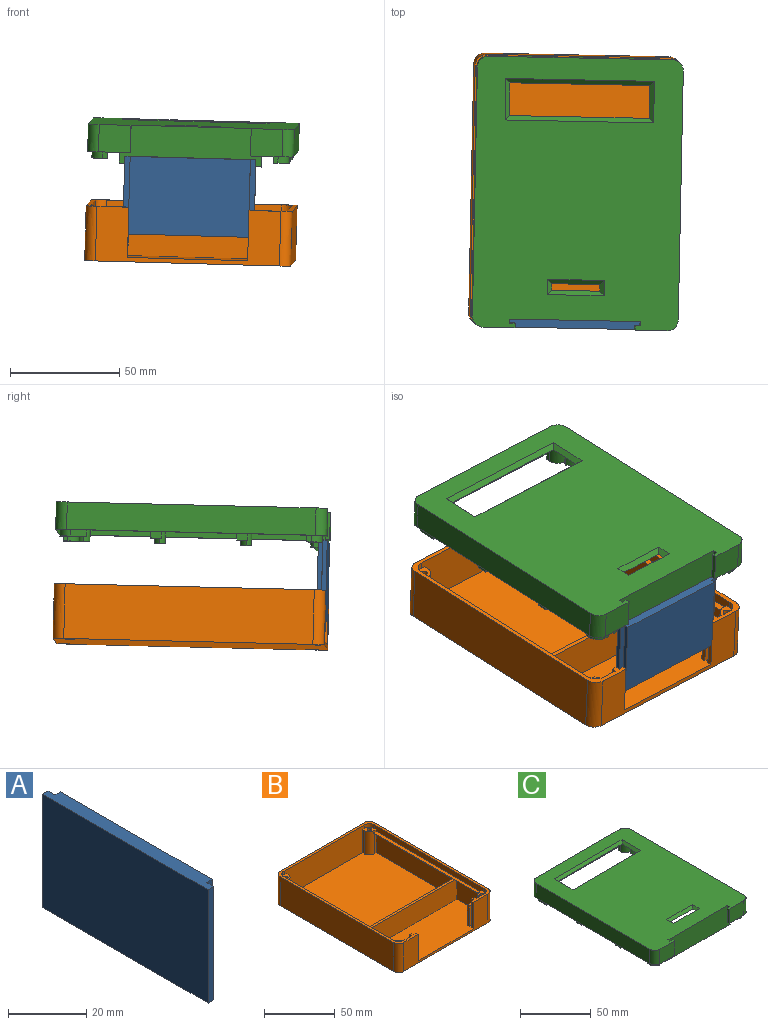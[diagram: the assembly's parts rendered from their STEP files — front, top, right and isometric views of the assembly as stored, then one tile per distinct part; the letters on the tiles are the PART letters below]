
ASSEMBLY  parts=3 mates=2
PART A: 10 faces, bbox 4x60x35.5 mm
  f0: plane 60x35.5mm, normal (-1,0,0), area 2130mm2, adj f1,f7,f8,f9
  f1: plane 35.5x2mm, normal (0,-1,0), area 71mm2, adj f0,f2,f8,f9
  f2: plane 35.5x2.5mm, normal (1,0,0), area 88.7mm2, adj f1,f3,f8,f9
  f3: plane 35.5x2mm, normal (0,-1,0), area 71mm2, adj f2,f4,f8,f9
  f4: plane 55x35.5mm, normal (1,0,0), area 1952.5mm2, adj f3,f5,f8,f9
  f5: plane 35.5x2mm, normal (0,1,0), area 71mm2, adj f4,f6,f8,f9
  f6: plane 35.5x2.5mm, normal (1,0,0), area 88.7mm2, adj f5,f7,f8,f9
  f7: plane 35.5x2mm, normal (0,1,0), area 71mm2, adj f0,f6,f8,f9
  f8: plane 60x4mm, normal (0,0,-1), area 230mm2, adj f0,f1,f2,f3,f4,f5,f6,f7
  f9: plane 60x4mm, normal (0,0,1), area 230mm2, adj f0,f1,f2,f3,f4,f5,f6,f7
PART B: 78 faces, bbox 94.2x124x25 mm
  f0: plane 124x94.2mm, normal (0,0,1), area 756.8mm2, adj f1,f3,f17,f20,f21,f22,f23,f24
  f1: plane 84.2x25mm, normal (0,-1,0), area 840mm2, adj f0,f5,f25,f30,f31,f68,f69
  f2: plane 18x5mm, normal (0,1,0), area 90mm2, adj f5,f62,f73,f75
  f3: plane 23x7.6mm, normal (0,1,0), area 134.8mm2, adj f0,f5,f38,f40,f55,f62
  f4: plane 25x15.5mm, normal (1,0,0), area 387.5mm2, adj f5,f8,f15,f59
  f5: plane 90.2x34mm, normal (0,0,1), area 2879.1mm2, adj f1,f2,f3,f4,f6,f12,f15,f20
  f6: plane 25x15.5mm, normal (-1,0,0), area 387.5mm2, adj f5,f7,f12,f59
  f7: plane 106.21x3.01mm, normal (-0.71,0,-0.71), area 442.7mm2, adj f6,f12,f18,f26,f44,f46,f48,f58
  f8: plane 106.21x3.01mm, normal (0.71,0,-0.71), area 442.7mm2, adj f4,f9,f14,f15,f45,f47,f49,f58
  f9: plane 17.5x2mm, normal (0,-1,0), area 33mm2, adj f8,f14,f19,f49
  f10: plane 2x1.5mm, normal (0,-1,0), area 3mm2, adj f17,f37,f44,f48
  f11: plane 2x1.5mm, normal (0,1,0), area 3mm2, adj f21,f43,f45,f47
  f12: plane 17.5x2mm, normal (0,1,0), area 33mm2, adj f5,f6,f7,f46
  f13: plane 2x1.5mm, normal (0,-1,0), area 3mm2, adj f21,f34,f45,f49
  f14: plane 79x15.5mm, normal (1,0,0), area 1224.5mm2, adj f8,f9,f19,f58
  f15: plane 17.5x2mm, normal (0,1,0), area 33mm2, adj f4,f5,f8,f47
  f16: plane 2x1.5mm, normal (0,1,0), area 3mm2, adj f17,f40,f44,f46
  f17: plane 110x4.5mm, normal (-1,0,0), area 489mm2, adj f0,f10,f16,f37,f40,f44,f55,f57
  f18: plane 17.5x2mm, normal (0,-1,0), area 33mm2, adj f7,f19,f26,f48
  f19: plane 90.2x86mm, normal (0,0,1), area 7669.9mm2, adj f9,f14,f18,f26,f27,f32,f35,f48
  f20: plane 23x7.6mm, normal (0,1,0), area 134.8mm2, adj f0,f5,f41,f43,f54,f61
  f21: plane 110x4.5mm, normal (1,0,0), area 489mm2, adj f0,f11,f13,f34,f43,f45,f54,f56
  f22: plane 114x25mm, normal (1,0,0), area 2850mm2, adj f0,f25,f28,f31
  f23: plane 84.2x25mm, normal (0,1,0), area 2105mm2, adj f0,f25,f28,f29
  f24: plane 114x25mm, normal (-1,0,0), area 2850mm2, adj f0,f25,f29,f30
  f25: plane 124x94.2mm, normal (0,0,-1), area 11404.9mm2, adj f1,f22,f23,f24,f28,f29,f30,f31
  f26: plane 79x15.5mm, normal (-1,0,0), area 1224.5mm2, adj f7,f18,f19,f58
  f27: plane 80.2x23mm, normal (0,-1,0), area 1764.6mm2, adj f0,f19,f32,f34,f35,f37,f56,f57
  f28: cylinder r=5mm len=25mm, axis (0,0,-1), area 196.3mm2, adj f0,f22,f23,f25
  f29: cylinder r=5mm len=25mm, axis (0,0,1), area 196.3mm2, adj f0,f23,f24,f25
  f30: cylinder r=5mm len=25mm, axis (0,0,-1), area 196.3mm2, adj f0,f1,f24,f25
  f31: cylinder r=5mm len=25mm, axis (0,0,1), area 196.3mm2, adj f0,f1,f22,f25
  f32: plane 20x2mm, normal (1,0,0), area 40mm2, adj f19,f27,f34,f49
  f33: cylinder r=1.5mm len=19mm, axis (0,0,-1), area 179.1mm2, adj f34,f50
  f34: plane 7x7mm, normal (0,0,1), area 31.2mm2, adj f13,f21,f27,f32,f33,f49,f56
  f35: plane 20x2mm, normal (-1,0,0), area 40mm2, adj f19,f27,f37,f48
  f36: cylinder r=1.5mm len=19mm, axis (0,0,-1), area 179.1mm2, adj f37,f51
  f37: plane 7x7mm, normal (0,0,1), area 31.2mm2, adj f10,f17,f27,f35,f36,f48,f57
  f38: plane 20x2mm, normal (-1,0,0), area 40mm2, adj f3,f5,f40,f46
  f39: cylinder r=1.5mm len=19mm, axis (0,0,-1), area 179.1mm2, adj f40,f52
  f40: plane 7x7mm, normal (0,0,1), area 31.2mm2, adj f3,f16,f17,f38,f39,f46,f55
  f41: plane 20x2mm, normal (1,0,0), area 40mm2, adj f5,f20,f43,f47
  f42: cylinder r=1.5mm len=19mm, axis (0,0,-1), area 179.1mm2, adj f43,f53
  f43: plane 7x7mm, normal (0,0,1), area 31.2mm2, adj f11,f20,f21,f41,f42,f47,f54
  f44: plane 106.2x3mm, normal (0,0,1), area 318.1mm2, adj f7,f10,f16,f17,f46,f48
  f45: plane 106.2x3mm, normal (0,0,1), area 318.1mm2, adj f8,f11,f13,f21,f47,f49
  f46: cylinder r=5mm len=20mm, axis (0,0,1), area 156.6mm2, adj f5,f7,f12,f16,f38,f40,f44
  f47: cylinder r=5mm len=20mm, axis (0,0,1), area 156.6mm2, adj f5,f8,f11,f15,f41,f43,f45
  f48: cylinder r=5mm len=20mm, axis (0,0,1), area 156.6mm2, adj f7,f10,f18,f19,f35,f37,f44
  f49: cylinder r=5mm len=20mm, axis (0,0,1), area 156.6mm2, adj f8,f9,f13,f19,f32,f34,f45
  f50: cone r=4.5mm half-angle=45deg, axis (0,0,-1), area 80mm2, adj f25,f33
  f51: cone r=4.5mm half-angle=45deg, axis (0,0,-1), area 80mm2, adj f25,f36
  f52: cone r=4.5mm half-angle=45deg, axis (0,0,-1), area 80mm2, adj f25,f39
  f53: cone r=4.5mm half-angle=45deg, axis (0,0,-1), area 80mm2, adj f25,f42
  f54: cylinder r=5mm len=5mm, axis (0,0,1), area 23.6mm2, adj f0,f20,f21,f43
  f55: cylinder r=5mm len=5mm, axis (0,0,-1), area 23.6mm2, adj f0,f3,f17,f40
  f56: cylinder r=5mm len=5mm, axis (0,0,-1), area 23.6mm2, adj f0,f21,f27,f34
  f57: cylinder r=5mm len=5mm, axis (0,0,1), area 23.6mm2, adj f0,f17,f27,f37
  f58: plane 90.2x18mm, normal (0,1,0), area 1617.4mm2, adj f7,f8,f14,f19,f26,f60
  f59: plane 90.2x18mm, normal (0,-1,0), area 1617.4mm2, adj f4,f5,f6,f7,f8,f60
  f60: plane 85.2x2mm, normal (0,0,1), area 170.4mm2, adj f7,f8,f58,f59
  f61: plane 23x4mm, normal (-1,0,0), area 82mm2, adj f0,f5,f20,f63,f76,f77
  f62: plane 23x4mm, normal (1,0,0), area 82mm2, adj f0,f2,f3,f5,f74,f75
  f63: plane 18x5mm, normal (0,1,0), area 90mm2, adj f5,f61,f64,f77
  f64: plane 18x2mm, normal (1,0,0), area 36mm2, adj f5,f63,f65,f77
  f65: plane 18x2.5mm, normal (0,-1,0), area 45mm2, adj f5,f64,f66,f77
  f66: plane 23x2mm, normal (1,0,0), area 46mm2, adj f0,f5,f65,f67,f76
  f67: plane 23x2.5mm, normal (0,1,0), area 57.5mm2, adj f0,f5,f66,f68
  f68: plane 23x2mm, normal (1,0,0), area 46mm2, adj f0,f1,f5,f67
  f69: plane 23x2mm, normal (-1,0,0), area 46mm2, adj f0,f1,f5,f70
  f70: plane 23x2.5mm, normal (0,1,0), area 57.5mm2, adj f0,f5,f69,f71
  f71: plane 23x2mm, normal (-1,0,0), area 46mm2, adj f0,f5,f70,f72,f74
  f72: plane 18x2.5mm, normal (0,-1,0), area 45mm2, adj f5,f71,f73,f75
  f73: plane 18x2mm, normal (-1,0,0), area 36mm2, adj f2,f5,f72,f75
  f74: plane 5x2.5mm, normal (0,1,0), area 12.5mm2, adj f0,f62,f71,f75
  f75: plane 5x2mm, normal (0,0,1), area 10mm2, adj f2,f62,f72,f73,f74
  f76: plane 5x2.5mm, normal (0,1,0), area 12.5mm2, adj f0,f61,f66,f77
  f77: plane 5x2mm, normal (0,0,1), area 10mm2, adj f61,f63,f64,f65,f76
PART C: 94 faces, bbox 94.2x124x17.5 mm
  f0: plane 29.5x10.5mm, normal (-1,0,0), area 309.7mm2, adj f4,f8,f82,f85
  f1: plane 29.5x10.5mm, normal (1,0,0), area 309.7mm2, adj f4,f8,f87,f90
  f2: plane 34.5x10.5mm, normal (1,0,0), area 362.3mm2, adj f4,f8,f86,f89
  f3: plane 34.5x10.5mm, normal (-1,0,0), area 362.3mm2, adj f4,f8,f84,f93
  f4: plane 124x94.2mm, normal (0,0,-1), area 756.1mm2, adj f0,f1,f2,f3,f5,f7,f9,f10
  f5: plane 14.52x12.5mm, normal (0,-1,0), area 181.5mm2, adj f4,f6,f20,f67
  f6: plane 124x94.2mm, normal (0,0,1), area 9954.6mm2, adj f5,f13,f14,f15,f16,f17,f18,f19
  f7: plane 10.5x5.6mm, normal (0,1,0), area 58.8mm2, adj f4,f8,f43,f64
  f8: plane 120x90.2mm, normal (0,0,-1), area 9292.7mm2, adj f0,f1,f2,f3,f7,f9,f10,f11
  f9: plane 27x10.5mm, normal (1,0,0), area 283.5mm2, adj f4,f8,f42,f88
  f10: plane 76.2x10.5mm, normal (0,-1,0), area 800.1mm2, adj f4,f8,f30,f36
  f11: plane 27x10.5mm, normal (-1,0,0), area 283.5mm2, adj f4,f8,f24,f92
  f12: plane 10.5x5.6mm, normal (0,1,0), area 58.8mm2, adj f4,f8,f23,f63
  f13: plane 113.84x12.5mm, normal (1,0,0), area 1423mm2, adj f4,f6,f17,f20
  f14: plane 84.04x12.5mm, normal (0,1,0), area 1050.5mm2, adj f4,f6,f17,f18
  f15: plane 113.84x12.5mm, normal (-1,0,0), area 1423mm2, adj f4,f6,f18,f19
  f16: plane 14.52x12.5mm, normal (0,-1,0), area 181.5mm2, adj f4,f6,f19,f68
  f17: cylinder r=5.08mm len=12.5mm, axis (0,0,-1), area 99.7mm2, adj f4,f6,f13,f14
  f18: cylinder r=5.08mm len=12.5mm, axis (0,0,1), area 99.7mm2, adj f4,f6,f14,f15
  f19: cylinder r=5.08mm len=12.5mm, axis (0,0,-1), area 99.7mm2, adj f4,f6,f15,f16
  f20: cylinder r=5.08mm len=12.5mm, axis (0,0,1), area 99.7mm2, adj f4,f5,f6,f13
  f21: plane 3x2mm, normal (0,-1,0), area 6mm2, adj f4,f23,f26,f62
  f22: plane 3x2mm, normal (1,0,0), area 6mm2, adj f4,f24,f26,f62
  f23: plane 13.5x2mm, normal (-1,0,0), area 27mm2, adj f8,f12,f21,f26,f50
  f24: plane 13.5x2mm, normal (0,1,0), area 27mm2, adj f8,f11,f22,f26,f50
  f25: cylinder r=1mm len=13.5mm, axis (0,0,1), area 84.8mm2, adj f26,f27
  f26: plane 7x7mm, normal (0,0,-1), area 35.1mm2, adj f21,f22,f23,f24,f25,f50,f62
  f27: plane 2x2mm, normal (0,0,-1), area 3.1mm2, adj f25
  f28: plane 3x2mm, normal (0,1,0), area 6mm2, adj f4,f30,f32,f61
  f29: plane 7x3mm, normal (1,0,0), area 21mm2, adj f4,f32,f61,f82
  f30: plane 13.5x2mm, normal (-1,0,0), area 27mm2, adj f8,f10,f28,f32,f49
  f31: cylinder r=1mm len=13.5mm, axis (0,0,1), area 84.8mm2, adj f32,f33
  f32: plane 12x7mm, normal (0,0,-1), area 48.3mm2, adj f28,f29,f30,f31,f49,f61,f82,f83
  f33: plane 2x2mm, normal (0,0,-1), area 3.1mm2, adj f31
  f34: plane 7x3mm, normal (-1,0,0), area 21mm2, adj f4,f38,f60,f90
  f35: plane 3x2mm, normal (0,1,0), area 6mm2, adj f4,f36,f38,f60
  f36: plane 13.5x2mm, normal (1,0,0), area 27mm2, adj f8,f10,f35,f38,f48
  f37: cylinder r=1mm len=13.5mm, axis (0,0,1), area 84.8mm2, adj f38,f39
  f38: plane 12x7mm, normal (0,0,-1), area 48.3mm2, adj f34,f35,f36,f37,f48,f60,f90,f91
  f39: plane 2x2mm, normal (0,0,-1), area 3.1mm2, adj f37
  f40: plane 3x2mm, normal (-1,0,0), area 6mm2, adj f4,f42,f45,f59
  f41: plane 3x2mm, normal (0,-1,0), area 6mm2, adj f4,f43,f45,f59
  f42: plane 13.5x2mm, normal (0,1,0), area 27mm2, adj f8,f9,f40,f45,f47
  f43: plane 13.5x2mm, normal (1,0,0), area 27mm2, adj f7,f8,f41,f45,f47
  f44: cylinder r=1mm len=13.5mm, axis (0,0,1), area 84.8mm2, adj f45,f46
  f45: plane 7x7mm, normal (0,0,-1), area 35.1mm2, adj f40,f41,f42,f43,f44,f47,f59
  f46: plane 2x2mm, normal (0,0,-1), area 3.1mm2, adj f44
  f47: cylinder r=5mm len=13.5mm, axis (0,0,1), area 106mm2, adj f8,f42,f43,f45
  f48: cylinder r=5mm len=13.5mm, axis (0,0,1), area 106mm2, adj f8,f36,f38,f91
  f49: cylinder r=5mm len=13.5mm, axis (0,0,1), area 106mm2, adj f8,f30,f32,f83
  f50: cylinder r=5mm len=13.5mm, axis (0,0,1), area 106mm2, adj f8,f23,f24,f26
  f51: plane 19x2mm, normal (-0.71,0,0.71), area 48.1mm2, adj f6,f8,f52,f54
  f52: plane 68x2mm, normal (0,0.71,0.71), area 186.7mm2, adj f6,f8,f51,f53
  f53: plane 19x2mm, normal (0.71,0,0.71), area 48.1mm2, adj f6,f8,f52,f54
  f54: plane 68x2mm, normal (0,-0.71,0.71), area 186.7mm2, adj f6,f8,f51,f53
  f55: plane 7x2mm, normal (-0.71,0,0.71), area 14.1mm2, adj f6,f8,f56,f58
  f56: plane 26x2mm, normal (0,0.71,0.71), area 67.9mm2, adj f6,f8,f55,f57
  f57: plane 7x2mm, normal (0.71,0,0.71), area 14.1mm2, adj f6,f8,f56,f58
  f58: plane 26x2mm, normal (0,-0.71,0.71), area 67.9mm2, adj f6,f8,f55,f57
  f59: cylinder r=5mm len=5mm, axis (0,0,1), area 23.6mm2, adj f4,f40,f41,f45
  f60: cylinder r=5mm len=5mm, axis (0,0,1), area 23.6mm2, adj f4,f34,f35,f38
  f61: cylinder r=5mm len=5mm, axis (0,0,1), area 23.6mm2, adj f4,f28,f29,f32
  f62: cylinder r=5mm len=5mm, axis (0,0,1), area 23.6mm2, adj f4,f21,f22,f26
  f63: plane 15.5x4mm, normal (1,0,0), area 52mm2, adj f4,f8,f12,f65,f71,f73
  f64: plane 15.5x4mm, normal (-1,0,0), area 52mm2, adj f4,f7,f8,f65,f71,f73
  f65: plane 65x15.5mm, normal (0,1,0), area 1007.5mm2, adj f8,f63,f64,f73
  f66: plane 12.5x2.5mm, normal (0,1,0), area 31.2mm2, adj f4,f6,f67,f72
  f67: plane 12.5x2mm, normal (-1,0,0), area 25mm2, adj f4,f5,f6,f66
  f68: plane 12.5x2mm, normal (1,0,0), area 25mm2, adj f4,f6,f16,f69
  f69: plane 12.5x2.5mm, normal (0,1,0), area 31.2mm2, adj f4,f6,f68,f70
  f70: plane 12.5x2mm, normal (1,0,0), area 25mm2, adj f4,f6,f69,f71
  f71: plane 65x17.5mm, normal (0,-1,0), area 1075mm2, adj f4,f6,f63,f64,f70,f72,f73
  f72: plane 12.5x2mm, normal (-1,0,0), area 25mm2, adj f4,f6,f66,f71
  f73: plane 65x2mm, normal (0,0,-1), area 130mm2, adj f63,f64,f65,f71
  f74: plane 5x3mm, normal (1,0,0), area 15mm2, adj f4,f75,f92,f93
  f75: plane 5x3.39mm, normal (0,0,-1), area 11.1mm2, adj f74,f92,f93
  f76: plane 5x3mm, normal (-1,0,0), area 15mm2, adj f4,f77,f88,f89
  f77: plane 5x3.39mm, normal (0,0,-1), area 11.1mm2, adj f76,f88,f89
  f78: plane 5x3mm, normal (-1,0,0), area 15mm2, adj f4,f79,f86,f87
  f79: plane 5x3.39mm, normal (0,0,-1), area 11.1mm2, adj f78,f86,f87
  f80: plane 5x3mm, normal (1,0,0), area 15mm2, adj f4,f81,f84,f85
  f81: plane 5x3.39mm, normal (0,0,-1), area 11.1mm2, adj f80,f84,f85
  f82: cylinder r=5mm len=13.5mm, axis (0,0,-1), area 65.4mm2, adj f0,f8,f29,f32,f83
  f83: cylinder r=5mm len=13.5mm, axis (0,0,1), area 35.6mm2, adj f8,f32,f49,f82
  f84: cylinder r=5mm len=13.5mm, axis (0,0,-1), area 58.7mm2, adj f3,f8,f80,f81,f85
  f85: cylinder r=5mm len=13.5mm, axis (0,0,1), area 58.7mm2, adj f0,f8,f80,f81,f84
  f86: cylinder r=5mm len=13.5mm, axis (0,0,-1), area 58.7mm2, adj f2,f8,f78,f79,f87
  f87: cylinder r=5mm len=13.5mm, axis (0,0,1), area 58.7mm2, adj f1,f8,f78,f79,f86
  f88: cylinder r=5mm len=13.5mm, axis (0,0,-1), area 58.7mm2, adj f8,f9,f76,f77,f89
  f89: cylinder r=5mm len=13.5mm, axis (0,0,1), area 58.7mm2, adj f2,f8,f76,f77,f88
  f90: cylinder r=5mm len=13.5mm, axis (0,0,-1), area 65.4mm2, adj f1,f8,f34,f38,f91
  f91: cylinder r=5mm len=13.5mm, axis (0,0,1), area 35.6mm2, adj f8,f38,f48,f90
  f92: cylinder r=5mm len=13.5mm, axis (0,0,-1), area 58.7mm2, adj f8,f11,f74,f75,f93
  f93: cylinder r=5mm len=13.5mm, axis (0,0,1), area 58.7mm2, adj f3,f8,f74,f75,f92
PLACE A rot(axis=(0,0.03,-1),91.2deg) t=(-317.84,2640.55,605.54)mm
PLACE B rot(axis=(0.58,0.66,-0.48),2.4deg) t=(-317.87,2701.65,560.78)mm
PLACE C rot(axis=(0.58,0.66,-0.48),2.4deg) t=(-316.52,2702.97,608.75)mm
MATE slider C.f26 <-> B.f40  axis (0.03,-0.02,1) through (-272.65,2646.69,603.18)mm
MATE slider A.f8 <-> B.f5  axis (0.03,-0.02,1) through (-346.32,2639.96,570.77)mm
